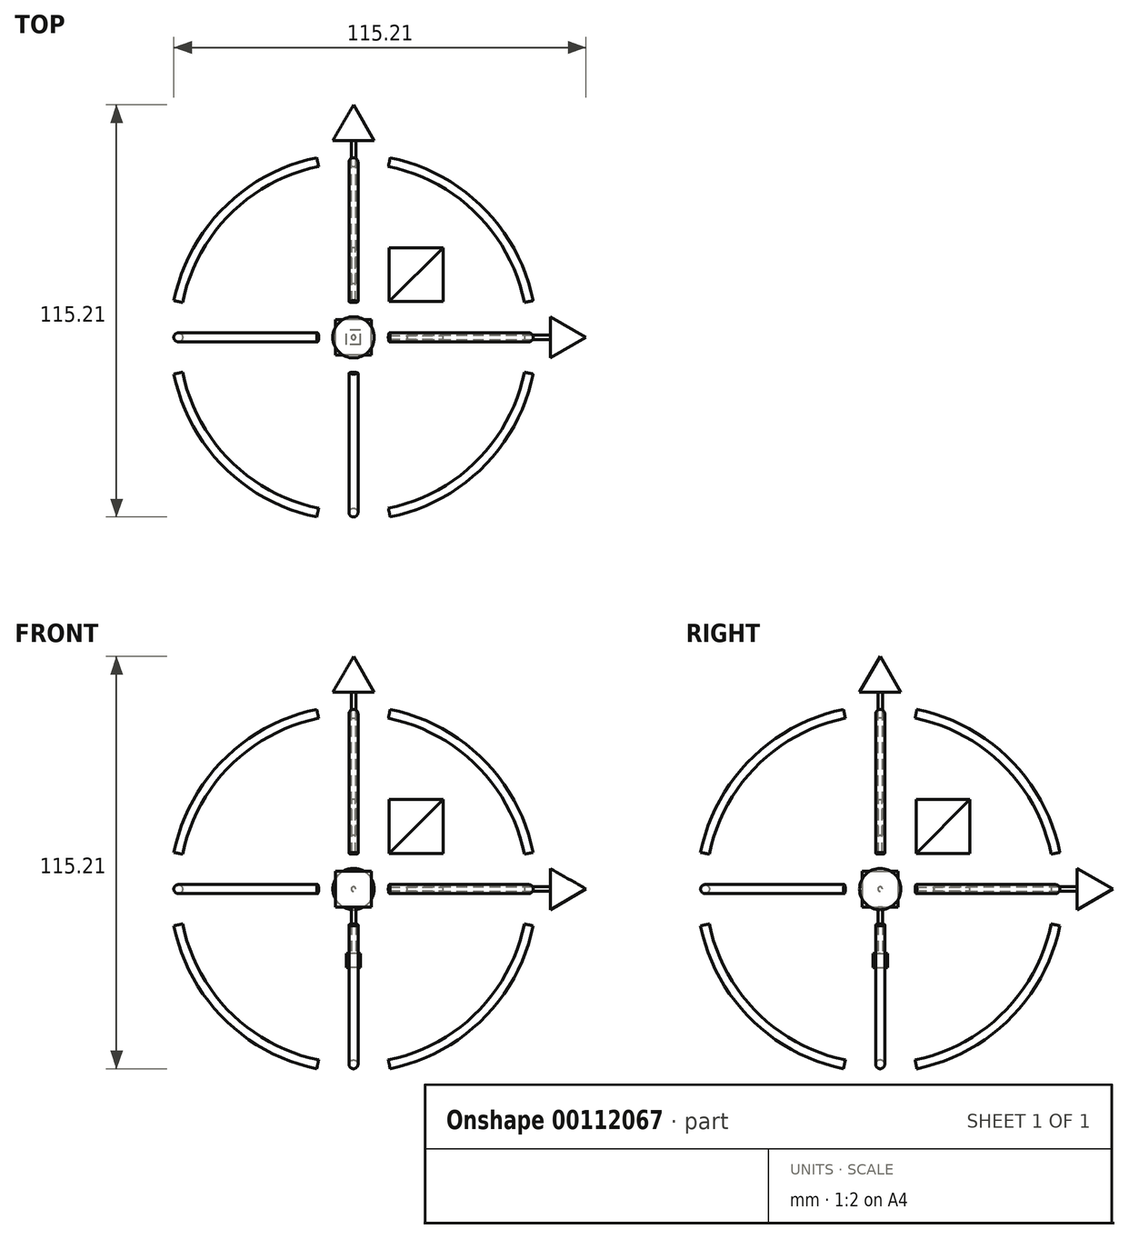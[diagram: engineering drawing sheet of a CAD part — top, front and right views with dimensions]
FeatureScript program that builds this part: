
annotation { "Feature Type Name" : "Feature", "Feature Type Description" : "" }
export const myFeature = defineFeature(function(context is Context, id is Id, definition is map)
    precondition{}
    {
        {
            var Q0;
            Q0=qCreatedBy(makeId("Top.planeOp"),FACE);
            var sketch = newSketch(context, id + "F0", { "sketchPlane" : qUnion([Q0])});
            skLineSegment(sketch, "E0", {"start": v(-37.81, 0) * mm, "end": v(46.13, 0) * mm, "construction": true});
            skSolve(sketch);
        }
        {
            var Q0;
            Q0=qCreatedBy(makeId("Top.planeOp"),FACE);
            var sketch = newSketch(context, id + "F1", { "sketchPlane" : qUnion([Q0])});
            skLineSegment(sketch, "E1", {"start": v(0, -30.5) * mm, "end": v(0, 59.13) * mm, "construction": true});
            skSolve(sketch);
        }
        {
            var Q0;
            Q0=qCreatedBy(makeId("Front.planeOp"),FACE);
            var sketch = newSketch(context, id + "F2", { "sketchPlane" : qUnion([Q0])});
            skLineSegment(sketch, "E2", {"start": v(0, -31.45) * mm, "end": v(0, 33.7) * mm, "construction": true});
            skSolve(sketch);
        }
        {
            var Q0;
            Q0=qCreatedBy(makeId("Front.planeOp"),FACE);
            var sketch = newSketch(context, id + "F3", { "sketchPlane" : qUnion([Q0])});
            skCircle(sketch, "E3", {"center": v(0, 0) * mm, "radius": 50 * mm, "construction": true});
            skLineSegment(sketch, "E4", {"start": v(0, 0) * mm, "end": v(0, 65) * mm, "construction": true});
            skLineSegment(sketch, "E5", {"start": v(0, 0) * mm, "end": v(0, -22) * mm, "construction": true});
            skSolve(sketch);
        }
        {
            var Q0;
            Q0=qCreatedBy(makeId("Front.planeOp"),FACE);
            var sketch = newSketch(context, id + "F4", { "sketchPlane" : qUnion([Q0])});
            skLineSegment(sketch, "E6", {"start": v(0, 65) * mm, "end": v(-5.77, 55) * mm});
            skLineSegment(sketch, "E7", {"start": v(-5.77, 55) * mm, "end": v(-0.63, 55) * mm});
            skLineSegment(sketch, "E8", {"start": v(-0.63, 55) * mm, "end": v(-0.63, 15) * mm});
            skLineSegment(sketch, "E9", {"start": v(0, 15) * mm, "end": v(-0.63, 15) * mm});
            skLineSegment(sketch, "E10", {"start": v(0, 65) * mm, "end": v(0, 15) * mm});
            skLineSegment(sketch, "E11", {"start": v(0, 55.13) * mm, "end": v(0, -65.59) * mm, "construction": true});
            skSolve(sketch);
        }
        {
            var Q0;
            Q0=makeQuery(id+"F4.imprint","IMPRINT",FACE,{"disambiguationData":[TD([[makeQuery(id+"F4.imprint","IMPRINT",EDGE,{"derivedFrom":sQuery(id+"F4.wireOp",EDGE,"E6")}),1.0]])]});
            var Q1;
            Q1=sQuery(id+"F4.wireOp",EDGE,"E10");
            var Q2;
            Q2=sQuery(id+"F4.wireOp",EDGE,"E10");
            revolve(context, id + "F5", {"entities" : qUnion([Q0]), "surfaceEntities" : qUnion([Q1]), "axis" : qUnion([Q2]), "revolveType" : RevolveType.FULL});
        }
        {
            var Q0;
            Q0=qCreatedBy(makeId("Front.planeOp"),FACE);
            var sketch = newSketch(context, id + "F6", { "sketchPlane" : qUnion([Q0])});
            skLineSegment(sketch, "E12.bottom", {"start": v(5, 5) * mm, "end": v(-5, 5) * mm});
            skLineSegment(sketch, "E12.top", {"start": v(5, -5) * mm, "end": v(-5, -5) * mm});
            skLineSegment(sketch, "E12.left", {"start": v(5, 5) * mm, "end": v(5, -5) * mm});
            skLineSegment(sketch, "E12.right", {"start": v(-5, 5) * mm, "end": v(-5, -5) * mm});
            skPoint(sketch, "E12.middle", {"position": v(0, 0) * mm});
            skSolve(sketch);
        }
        {
            var Q0;
            Q0 = qSketchRegion(id + "F6", true);
            extrude(context, id + "F7", {"entities" : qUnion([Q0]), "endBound" : BoundingType.SYMMETRIC, "depth" : 10 * mm});
        }
        {
            var Q0;
            Q0=qCreatedBy(makeId("Front.planeOp"),FACE);
            var sketch = newSketch(context, id + "F8", { "sketchPlane" : qUnion([Q0])});
            skLineSegment(sketch, "E13.bottom", {"start": v(2, -22) * mm, "end": v(-2, -22) * mm});
            skLineSegment(sketch, "E13.top", {"start": v(2, -18) * mm, "end": v(-2, -18) * mm});
            skLineSegment(sketch, "E13.left", {"start": v(2, -22) * mm, "end": v(2, -18) * mm});
            skLineSegment(sketch, "E13.right", {"start": v(-2, -22) * mm, "end": v(-2, -18) * mm});
            skPoint(sketch, "E13.middle", {"position": v(0, -20) * mm});
            skSolve(sketch);
        }
        {
            var Q0;
            Q0 = qSketchRegion(id + "F8", true);
            extrude(context, id + "F9", {"entities" : qUnion([Q0]), "endBound" : BoundingType.SYMMETRIC, "depth" : 4 * mm});
        }
        {
            var Q0;
            Q0=makeQuery(id+"F9.opExtrude","SWEPT_FACE",FACE,{"disambiguationData":[OSD([sQuery(id+"F8.wireOp",EDGE,"E13.top")])]});
            var sketch = newSketch(context, id + "F10", { "sketchPlane" : qUnion([Q0])});
            skCircle(sketch, "E14", {"center": v(0, 0) * mm, "radius": 0.62 * mm});
            skSolve(sketch);
        }
        {
            var Q0;
            Q0 = qSketchRegion(id + "F10", true);
            var Q1;
            Q1=qCreatedBy(makeId("Top.planeOp"),FACE);
            extrude(context, id + "F11", {"entities" : qUnion([Q0]), "operationType" : NewBodyOperationType.ADD, "endBound" : BoundingType.UP_TO_SURFACE, "endBoundEntityFace" : qUnion([Q1]), "depth" : 25 * mm});
        }
        {
            var Q0;
            Q0=makeQuery(id+"F5.opRevolve","SWEPT_BODY",BODY,{"disambiguationData":[OSD([sQuery(id+"F4.wireOp",EDGE,"E6"),sQuery(id+"F4.wireOp",EDGE,"E7"),sQuery(id+"F4.wireOp",EDGE,"E8"),sQuery(id+"F4.wireOp",EDGE,"E9"),sQuery(id+"F4.wireOp",EDGE,"E10")])]});
            var Q1;
            Q1=makeQuery(id+"F9.opExtrude","SWEPT_BODY",BODY,{"disambiguationData":[OSD([sQuery(id+"F8.wireOp",EDGE,"E13.bottom"),sQuery(id+"F8.wireOp",EDGE,"E13.top"),sQuery(id+"F8.wireOp",EDGE,"E13.left"),sQuery(id+"F8.wireOp",EDGE,"E13.right")])]});
            var Q2;
            Q2=sQuery(id+"F1.wireOp",EDGE,"E1");
            circularPattern(context, id + "F12", {"entities" : qUnion([Q0, Q1]), "axis" : qUnion([Q2]), "angle" : 90 * degree, "instanceCount" : 2});
        }
        {
            var Q0;
            Q0=makeQuery(id+"F5.opRevolve","SWEPT_BODY",BODY,{"disambiguationData":[OSD([sQuery(id+"F4.wireOp",EDGE,"E6"),sQuery(id+"F4.wireOp",EDGE,"E7"),sQuery(id+"F4.wireOp",EDGE,"E8"),sQuery(id+"F4.wireOp",EDGE,"E9"),sQuery(id+"F4.wireOp",EDGE,"E10")])]});
            var Q1;
            Q1=makeQuery(id+"F9.opExtrude","SWEPT_BODY",BODY,{"disambiguationData":[OSD([sQuery(id+"F8.wireOp",EDGE,"E13.bottom"),sQuery(id+"F8.wireOp",EDGE,"E13.top"),sQuery(id+"F8.wireOp",EDGE,"E13.left"),sQuery(id+"F8.wireOp",EDGE,"E13.right")])]});
            var Q2;
            Q2=sQuery(id+"F0.wireOp",EDGE,"E0");
            circularPattern(context, id + "F13", {"entities" : qUnion([Q0, Q1]), "axis" : qUnion([Q2]), "angle" : 90 * degree, "instanceCount" : 2, "oppositeDirection" : true});
        }
        {
            var Q0;
            Q0=qCreatedBy(makeId("Front.planeOp"),FACE);
            var sketch = newSketch(context, id + "F14", { "sketchPlane" : qUnion([Q0])});
            skArc(sketch, "E15.0", {"start": v(-10, 48.99) * mm, "mid": v(-35.36, 35.36) * mm, "end": v(-48.99, 10) * mm});
            skLineSegment(sketch, "E16.0", {"start": v(0, -31.45) * mm, "end": v(0, 33.7) * mm, "construction": true});
            skLineSegment(sketch, "E17", {"start": v(0, 0) * mm, "end": v(-40.84, 40.84) * mm, "construction": true});
            skSolve(sketch);
        }
        {
            var Q0;
            Q0=sQuery(id+"F14.wireOp",EDGE,"E15.0");
            var Q1;
            Q1=sQuery(id+"F14.wireOp",VERTEX,"E15.0.start");
            cPlane(context, id + "F15", {"entities" : qUnion([Q0, Q1]), "cplaneType" : CPlaneType.CURVE_POINT, "offset" : 25 * mm, "width" : 150 * mm, "height" : 150 * mm});
        }
        {
            var Q0;
            Q0=qCreatedBy(id+"F15.planeOp",FACE);
            var sketch = newSketch(context, id + "F16", { "sketchPlane" : qUnion([Q0])});
            skCircle(sketch, "E18", {"center": v(0, 50) * mm, "radius": 1.25 * mm});
            skSolve(sketch);
        }
        {
            var Q0;
            Q0=makeQuery(id+"F16.imprint","IMPRINT",FACE,{"disambiguationData":[TD([[makeQuery(id+"F16.imprint","IMPRINT",EDGE,{"derivedFrom":sQuery(id+"F16.wireOp",EDGE,"E18")}),1.0]])]});
            var Q1;
            Q1=sQuery(id+"F14.wireOp",EDGE,"E15.0");
            sweep(context, id + "F17", {"profiles" : qUnion([Q0]), "path" : qUnion([Q1])});
        }
        {
            var Q0;
            Q0=makeQuery(id+"F17.opSweep","SWEPT_BODY",BODY,{"disambiguationData":[OSD([sQuery(id+"F14.wireOp",EDGE,"E15.0"),sQuery(id+"F16.wireOp",EDGE,"E18")])]});
            var Q1;
            Q1=sQuery(id+"F1.wireOp",EDGE,"E1");
            circularPattern(context, id + "F18", {"entities" : qUnion([Q0]), "axis" : qUnion([Q1]), "angle" : 360 * degree, "instanceCount" : 4, "equalSpace" : true});
        }
        {
            var Q0;
            Q0=makeQuery(id+"F17.opSweep","SWEPT_BODY",BODY,{"disambiguationData":[OSD([sQuery(id+"F14.wireOp",EDGE,"E15.0"),sQuery(id+"F16.wireOp",EDGE,"E18")])]});
            var Q1;
            Q1=makeQuery(id+"F18.opPattern","COPY",BODY,{"derivedFrom":makeQuery(id+"F17.opSweep","SWEPT_BODY",BODY,{"disambiguationData":[OSD([sQuery(id+"F14.wireOp",EDGE,"E15.0"),sQuery(id+"F16.wireOp",EDGE,"E18")])]}),"instanceName":"3"});
            var Q2;
            Q2=makeQuery(id+"F18.opPattern","COPY",BODY,{"derivedFrom":makeQuery(id+"F17.opSweep","SWEPT_BODY",BODY,{"disambiguationData":[OSD([sQuery(id+"F14.wireOp",EDGE,"E15.0"),sQuery(id+"F16.wireOp",EDGE,"E18")])]}),"instanceName":"1"});
            var Q3;
            Q3=makeQuery(id+"F18.opPattern","COPY",BODY,{"derivedFrom":makeQuery(id+"F17.opSweep","SWEPT_BODY",BODY,{"disambiguationData":[OSD([sQuery(id+"F14.wireOp",EDGE,"E15.0"),sQuery(id+"F16.wireOp",EDGE,"E18")])]}),"instanceName":"2"});
            var Q4;
            Q4=sQuery(id+"F2.wireOp",EDGE,"E2");
            circularPattern(context, id + "F19", {"entities" : qUnion([Q0, Q1, Q2, Q3]), "axis" : qUnion([Q4]), "angle" : 90 * degree, "instanceCount" : 2});
        }
        {
            var Q0;
            Q0=makeQuery(id+"F19.opPattern","COPY",BODY,{"derivedFrom":makeQuery(id+"F17.opSweep","SWEPT_BODY",BODY,{"disambiguationData":[OSD([sQuery(id+"F14.wireOp",EDGE,"E15.0"),sQuery(id+"F16.wireOp",EDGE,"E18")])]}),"instanceName":"1"});
            var Q1;
            Q1=makeQuery(id+"F19.opPattern","COPY",BODY,{"derivedFrom":makeQuery(id+"F18.opPattern","COPY",BODY,{"derivedFrom":makeQuery(id+"F17.opSweep","SWEPT_BODY",BODY,{"disambiguationData":[OSD([sQuery(id+"F14.wireOp",EDGE,"E15.0"),sQuery(id+"F16.wireOp",EDGE,"E18")])]}),"instanceName":"3"}),"instanceName":"1"});
            var Q2;
            Q2=makeQuery(id+"F19.opPattern","COPY",BODY,{"derivedFrom":makeQuery(id+"F18.opPattern","COPY",BODY,{"derivedFrom":makeQuery(id+"F17.opSweep","SWEPT_BODY",BODY,{"disambiguationData":[OSD([sQuery(id+"F14.wireOp",EDGE,"E15.0"),sQuery(id+"F16.wireOp",EDGE,"E18")])]}),"instanceName":"2"}),"instanceName":"1"});
            var Q3;
            Q3=makeQuery(id+"F19.opPattern","COPY",BODY,{"derivedFrom":makeQuery(id+"F18.opPattern","COPY",BODY,{"derivedFrom":makeQuery(id+"F17.opSweep","SWEPT_BODY",BODY,{"disambiguationData":[OSD([sQuery(id+"F14.wireOp",EDGE,"E15.0"),sQuery(id+"F16.wireOp",EDGE,"E18")])]}),"instanceName":"1"}),"instanceName":"1"});
            var Q4;
            Q4=sQuery(id+"F1.wireOp",EDGE,"E1");
            circularPattern(context, id + "F20", {"entities" : qUnion([Q0, Q1, Q2, Q3]), "axis" : qUnion([Q4]), "angle" : 90 * degree, "instanceCount" : 2});
        }
        {
            var Q0;
            Q0=qCreatedBy(makeId("Front.planeOp"),FACE);
            var sketch = newSketch(context, id + "F21", { "sketchPlane" : qUnion([Q0])});
            skLineSegment(sketch, "E19.bottom", {"start": v(25, 25) * mm, "end": v(10, 25) * mm});
            skLineSegment(sketch, "E19.top", {"start": v(25, 10) * mm, "end": v(10, 10) * mm});
            skLineSegment(sketch, "E19.left", {"start": v(25, 25) * mm, "end": v(25, 10) * mm});
            skLineSegment(sketch, "E19.right", {"start": v(10, 25) * mm, "end": v(10, 10) * mm});
            skPoint(sketch, "E19.middle", {"position": v(17.5, 17.5) * mm});
            skLineSegment(sketch, "E20", {"start": v(10, 10) * mm, "end": v(0, 10) * mm, "construction": true});
            skLineSegment(sketch, "E21", {"start": v(10, 10) * mm, "end": v(10, 0) * mm, "construction": true});
            skLineSegment(sketch, "E22", {"start": v(10, 10) * mm, "end": v(25, 25) * mm});
            skSolve(sketch);
        }
        {
            var Q0;
            Q0=makeQuery(id+"F21.imprint","IMPRINT",FACE,{"disambiguationData":[TD([[makeQuery(id+"F21.imprint","IMPRINT",EDGE,{"derivedFrom":sQuery(id+"F21.wireOp",EDGE,"E19.bottom")}),1.0]])]});
            extrude(context, id + "F22", {"entities" : qUnion([Q0]), "endBound" : BoundingType.SYMMETRIC, "depth" : 1 * mm});
        }
        {
            var Q0;
            Q0=makeQuery(id+"F22.opExtrude","SWEPT_BODY",BODY,{"disambiguationData":[OSD([sQuery(id+"F21.wireOp",EDGE,"E19.bottom"),sQuery(id+"F21.wireOp",EDGE,"E19.right"),sQuery(id+"F21.wireOp",EDGE,"E22")])]});
            var Q1;
            Q1=makeQuery(id+"F22.opExtrude","SWEPT_FACE",FACE,{"disambiguationData":[OSD([sQuery(id+"F21.wireOp",EDGE,"E22")])]});
            mirror(context, id + "F23", {"entities" : qUnion([Q0]), "mirrorPlane" : qUnion([Q1])});
        }
        {
            var Q0;
            Q0=makeQuery(id+"F22.opExtrude","SWEPT_BODY",BODY,{"disambiguationData":[OSD([sQuery(id+"F21.wireOp",EDGE,"E19.bottom"),sQuery(id+"F21.wireOp",EDGE,"E19.right"),sQuery(id+"F21.wireOp",EDGE,"E22")])]});
            var Q1;
            Q1=makeQuery(id+"F23.opPattern","COPY",BODY,{"derivedFrom":makeQuery(id+"F22.opExtrude","SWEPT_BODY",BODY,{"disambiguationData":[OSD([sQuery(id+"F21.wireOp",EDGE,"E19.bottom"),sQuery(id+"F21.wireOp",EDGE,"E19.right"),sQuery(id+"F21.wireOp",EDGE,"E22")])]}),"instanceName":"1"});
            var Q2;
            Q2=sQuery(id+"F2.wireOp",EDGE,"E2");
            circularPattern(context, id + "F24", {"entities" : qUnion([Q0, Q1]), "axis" : qUnion([Q2]), "angle" : 90 * degree, "instanceCount" : 2});
        }
        {
            var Q0;
            Q0=makeQuery(id+"F24.opPattern","COPY",BODY,{"derivedFrom":makeQuery(id+"F22.opExtrude","SWEPT_BODY",BODY,{"disambiguationData":[OSD([sQuery(id+"F21.wireOp",EDGE,"E19.bottom"),sQuery(id+"F21.wireOp",EDGE,"E19.right"),sQuery(id+"F21.wireOp",EDGE,"E22")])]}),"instanceName":"1"});
            var Q1;
            Q1=makeQuery(id+"F24.opPattern","COPY",BODY,{"derivedFrom":makeQuery(id+"F23.opPattern","COPY",BODY,{"derivedFrom":makeQuery(id+"F22.opExtrude","SWEPT_BODY",BODY,{"disambiguationData":[OSD([sQuery(id+"F21.wireOp",EDGE,"E19.bottom"),sQuery(id+"F21.wireOp",EDGE,"E19.right"),sQuery(id+"F21.wireOp",EDGE,"E22")])]}),"instanceName":"1"}),"instanceName":"1"});
            var Q2;
            Q2=sQuery(id+"F1.wireOp",EDGE,"E1");
            circularPattern(context, id + "F25", {"entities" : qUnion([Q0, Q1]), "axis" : qUnion([Q2]), "angle" : 90 * degree, "instanceCount" : 2});
        }
    });
